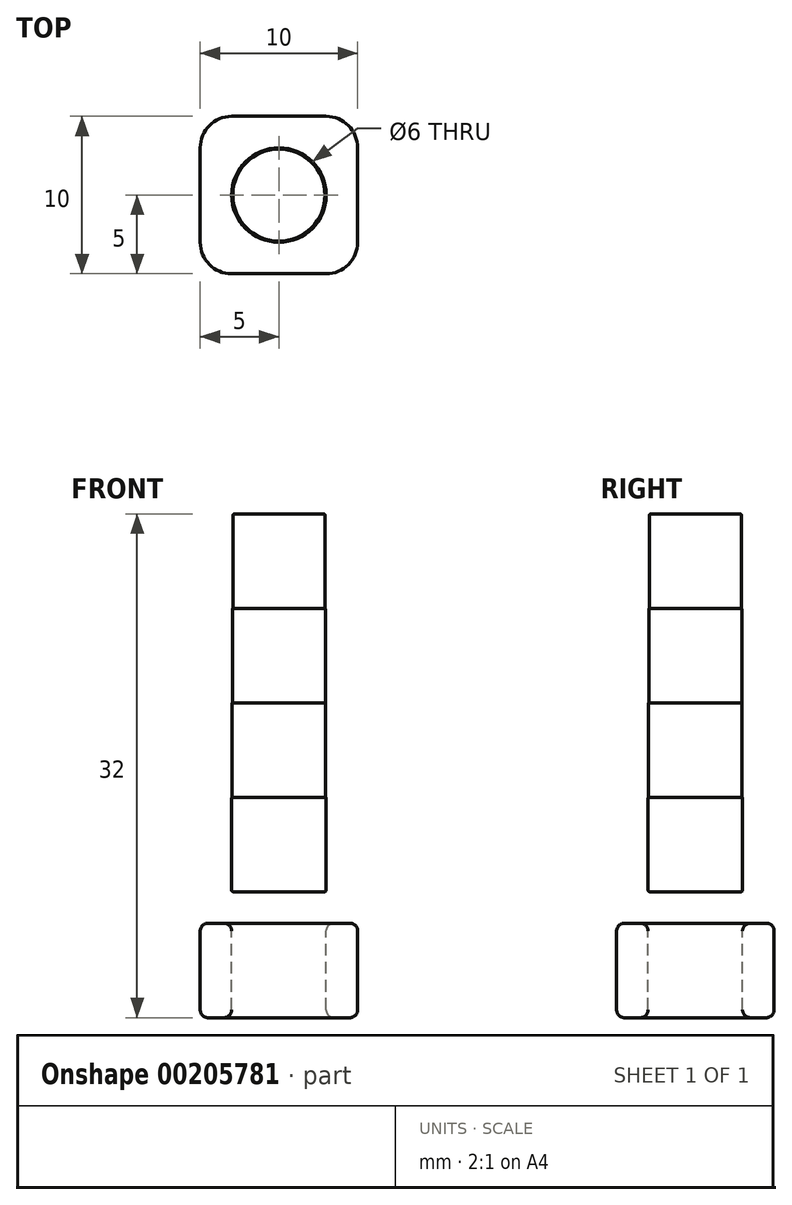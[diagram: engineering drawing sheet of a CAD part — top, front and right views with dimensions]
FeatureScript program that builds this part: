
annotation { "Feature Type Name" : "Feature", "Feature Type Description" : "" }
export const myFeature = defineFeature(function(context is Context, id is Id, definition is map)
    precondition{}
    {
        {
            var Q0;
            Q0=qCreatedBy(makeId("Top.planeOp"),FACE);
            var sketch = newSketch(context, id + "F0", { "sketchPlane" : qUnion([Q0])});
            skCircle(sketch, "E0", {"center": v(0, 0) * mm, "radius": 3 * mm});
            skLineSegment(sketch, "E1.bottom", {"start": v(5, 5) * mm, "end": v(-5, 5) * mm});
            skLineSegment(sketch, "E1.top", {"start": v(5, -5) * mm, "end": v(-5, -5) * mm});
            skLineSegment(sketch, "E1.left", {"start": v(5, 5) * mm, "end": v(5, -5) * mm});
            skLineSegment(sketch, "E1.right", {"start": v(-5, 5) * mm, "end": v(-5, -5) * mm});
            skPoint(sketch, "E2", {"position": v(0, 3) * mm});
            skSolve(sketch);
        }
        {
            var Q0;
            Q0 = qSketchRegion(id + "F0", true);
            extrude(context, id + "F1", {"entities" : qUnion([Q0]), "oppositeDirection" : true, "depth" : 6 * mm});
        }
        {
            var Q0;
            Q0=makeQuery(id+"F1.opExtrude","CAP_EDGE",EDGE,{"disambiguationData":[OSD([sQuery(id+"F0.wireOp",EDGE,"E0")])],"isStart":false});
            var Q1;
            Q1=makeQuery(id+"F1.opExtrude","CAP_EDGE",EDGE,{"disambiguationData":[OSD([sQuery(id+"F0.wireOp",EDGE,"E0")])],"isStart":true});
            fillet(context, id + "F2", {"entities" : qUnion([Q0, Q1]), "radius" : .5 * mm, "tangentPropagation" : true, "allowEdgeOverflow" : false});
        }
        {
            var Q0;
            Q0=makeQuery(id+"F1.opExtrude","SWEPT_EDGE",EDGE,{"disambiguationData":[OSD([sQuery(id+"F0.wireOp",EDGE,"E1.top"),sQuery(id+"F0.wireOp",EDGE,"E1.right")])]});
            var Q1;
            Q1=makeQuery(id+"F1.opExtrude","SWEPT_EDGE",EDGE,{"disambiguationData":[OSD([sQuery(id+"F0.wireOp",EDGE,"E1.top"),sQuery(id+"F0.wireOp",EDGE,"E1.left")])]});
            var Q2;
            Q2=makeQuery(id+"F1.opExtrude","SWEPT_EDGE",EDGE,{"disambiguationData":[OSD([sQuery(id+"F0.wireOp",EDGE,"E1.bottom"),sQuery(id+"F0.wireOp",EDGE,"E1.right")])]});
            var Q3;
            Q3=makeQuery(id+"F1.opExtrude","SWEPT_EDGE",EDGE,{"disambiguationData":[OSD([sQuery(id+"F0.wireOp",EDGE,"E1.bottom"),sQuery(id+"F0.wireOp",EDGE,"E1.left")])]});
            fillet(context, id + "F3", {"entities" : qUnion([Q0, Q1, Q2, Q3]), "radius" : 2 * mm, "tangentPropagation" : true, "allowEdgeOverflow" : false});
        }
        {
            var Q0;
            {var subQ0=sQuery(id+"F0.wireOp",EDGE,"E1.right");var subQ1=sQuery(id+"F0.wireOp",EDGE,"E1.top");Q0=makeQuery(id+"F3.opFillet","BLEND_EDGE",EDGE,{"blendedFrom":[makeQuery(id+"F1.opExtrude","SWEPT_EDGE",EDGE,{"disambiguationData":[OSD([subQ1,subQ0])]}),makeQuery(id+"F1.opExtrude","CAP_FACE",FACE,{"disambiguationData":[OSD([sQuery(id+"F0.wireOp",EDGE,"E0"),sQuery(id+"F0.wireOp",EDGE,"E1.bottom"),subQ1,sQuery(id+"F0.wireOp",EDGE,"E1.left"),subQ0])],"isStart":false})],"blendedInto":[makeQuery(id+"F1.opExtrude","CAP_FACE",FACE,{"disambiguationData":[OSD([sQuery(id+"F0.wireOp",EDGE,"E0"),sQuery(id+"F0.wireOp",EDGE,"E1.bottom"),subQ1,sQuery(id+"F0.wireOp",EDGE,"E1.left"),subQ0])],"isStart":false})]});}
            var Q1;
            {var subQ0=sQuery(id+"F0.wireOp",EDGE,"E1.right");var subQ1=sQuery(id+"F0.wireOp",EDGE,"E1.top");Q1=makeQuery(id+"F3.opFillet","BLEND_EDGE",EDGE,{"blendedFrom":[makeQuery(id+"F1.opExtrude","SWEPT_EDGE",EDGE,{"disambiguationData":[OSD([subQ1,subQ0])]}),makeQuery(id+"F1.opExtrude","CAP_FACE",FACE,{"disambiguationData":[OSD([sQuery(id+"F0.wireOp",EDGE,"E0"),sQuery(id+"F0.wireOp",EDGE,"E1.bottom"),subQ1,sQuery(id+"F0.wireOp",EDGE,"E1.left"),subQ0])],"isStart":true})],"blendedInto":[makeQuery(id+"F1.opExtrude","CAP_FACE",FACE,{"disambiguationData":[OSD([sQuery(id+"F0.wireOp",EDGE,"E0"),sQuery(id+"F0.wireOp",EDGE,"E1.bottom"),subQ1,sQuery(id+"F0.wireOp",EDGE,"E1.left"),subQ0])],"isStart":true})]});}
            fillet(context, id + "F4", {"entities" : qUnion([Q0, Q1]), "radius" : .5 * mm, "tangentPropagation" : true, "allowEdgeOverflow" : false});
        }
        {
            var Q0;
            Q0=qCreatedBy(makeId("Front.planeOp"),FACE);
            var sketch = newSketch(context, id + "F5", { "sketchPlane" : qUnion([Q0])});
            skLineSegment(sketch, "E3", {"start": v(0, 0) * mm, "end": v(0, 26) * mm, "construction": true});
            skLineSegment(sketch, "E4", {"start": v(0, 26) * mm, "end": v(-2.93, 26) * mm});
            skLineSegment(sketch, "E5", {"start": v(-2.93, 26) * mm, "end": v(-2.93, 20) * mm});
            skLineSegment(sketch, "E6", {"start": v(-2.95, 20) * mm, "end": v(-2.93, 20) * mm});
            skLineSegment(sketch, "E7", {"start": v(-2.95, 20) * mm, "end": v(-2.95, 14) * mm});
            skLineSegment(sketch, "E8", {"start": v(-2.98, 14) * mm, "end": v(-2.95, 14) * mm});
            skLineSegment(sketch, "E9", {"start": v(-2.98, 14) * mm, "end": v(-2.98, 8) * mm});
            skLineSegment(sketch, "E10", {"start": v(-3, 8) * mm, "end": v(-2.98, 8) * mm});
            skLineSegment(sketch, "E11", {"start": v(-3, 8) * mm, "end": v(-3, 2) * mm});
            skLineSegment(sketch, "E12", {"start": v(-3, 2) * mm, "end": v(0, 2) * mm});
            skLineSegment(sketch, "E13", {"start": v(-3, 2) * mm, "end": v(-3, 0) * mm, "construction": true});
            skLineSegment(sketch, "E14", {"start": v(0, 26) * mm, "end": v(0, 2) * mm});
            skSolve(sketch);
        }
        {
            var Q0;
            Q0=makeQuery(id+"F5.imprint","IMPRINT",FACE,{"disambiguationData":[TD([[makeQuery(id+"F5.imprint","IMPRINT",EDGE,{"derivedFrom":sQuery(id+"F5.wireOp",EDGE,"E4")}),1.0]])]});
            var Q1;
            Q1=sQuery(id+"F5.wireOp",EDGE,"E14");
            revolve(context, id + "F6", {"entities" : qUnion([Q0]), "axis" : qUnion([Q1]), "revolveType" : RevolveType.FULL});
        }
        {
            var Q0;
            Q0=makeQuery(id+"F6.opRevolve","SWEPT_EDGE",EDGE,{"disambiguationData":[OSD([sQuery(id+"F5.wireOp",EDGE,"E6"),sQuery(id+"F5.wireOp",EDGE,"E7")])]});
            var Q1;
            Q1=makeQuery(id+"F6.opRevolve","SWEPT_EDGE",EDGE,{"disambiguationData":[OSD([sQuery(id+"F5.wireOp",EDGE,"E8"),sQuery(id+"F5.wireOp",EDGE,"E9")])]});
            var Q2;
            Q2=makeQuery(id+"F6.opRevolve","SWEPT_EDGE",EDGE,{"disambiguationData":[OSD([sQuery(id+"F5.wireOp",EDGE,"E10"),sQuery(id+"F5.wireOp",EDGE,"E11")])]});
            var Q3;
            Q3=makeQuery(id+"F6.opRevolve","SWEPT_EDGE",EDGE,{"disambiguationData":[OSD([sQuery(id+"F5.wireOp",EDGE,"E4"),sQuery(id+"F5.wireOp",EDGE,"E5")])]});
            var Q4;
            Q4=makeQuery(id+"F6.opRevolve","SWEPT_EDGE",EDGE,{"disambiguationData":[OSD([sQuery(id+"F5.wireOp",EDGE,"E11"),sQuery(id+"F5.wireOp",EDGE,"E12")])]});
            fillet(context, id + "F7", {"entities" : qUnion([Q0, Q1, Q2, Q3, Q4]), "radius" : .1 * mm, "tangentPropagation" : true, "allowEdgeOverflow" : false});
        }
    });
